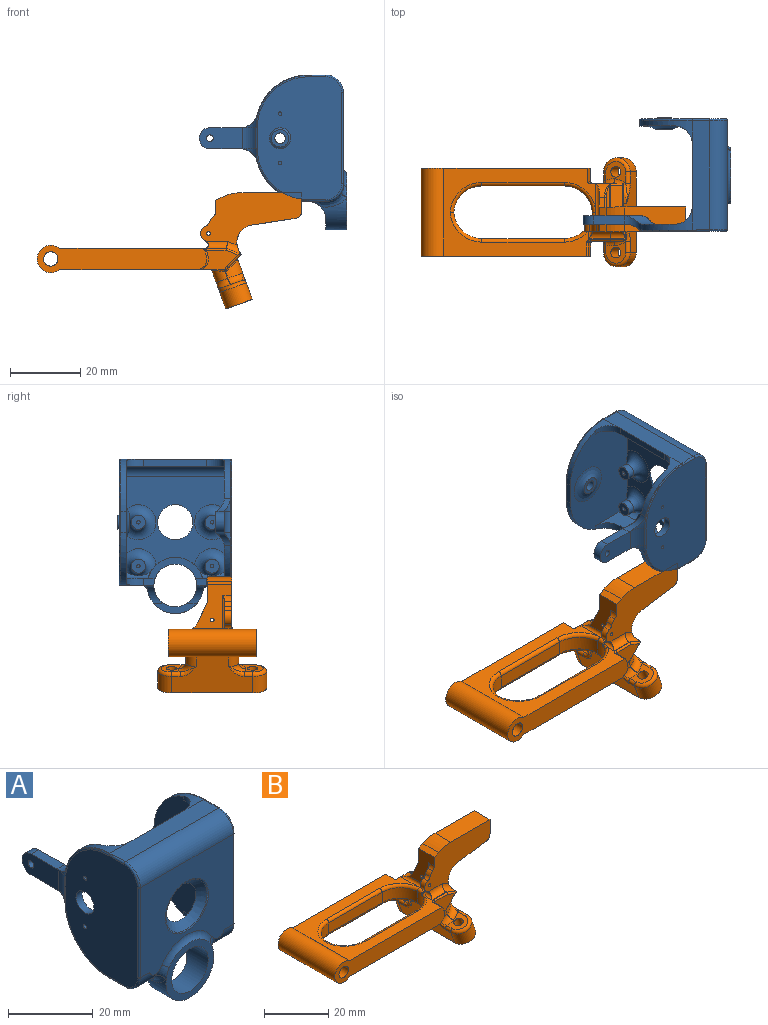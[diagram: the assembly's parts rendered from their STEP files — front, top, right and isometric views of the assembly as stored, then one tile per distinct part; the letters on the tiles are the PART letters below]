
ASSEMBLY  parts=2 mates=1
PART A: 112 faces, bbox 37.6x43.4x49.7 mm
  f0: plane 34.28x22.36mm, normal (1,0,0), area 579.8mm2, adj f18,f21,f30,f32,f33,f34,f36,f37
  f1: cylinder r=5mm len=6.53mm, axis (1,0,0), area 41.7mm2, adj f8,f9,f23,f66,f86,f87
  f2: cylinder r=5mm len=0.6mm, axis (1,0,0), area 0.1mm2, adj f9,f39,f89
  f3: plane 7.91x5.41mm, normal (0,0,-1), area 34.3mm2, adj f6,f20,f28,f70,f90
  f4: plane 3.24x2mm, normal (0,1,0), area 6mm2, adj f23,f30,f36,f80,f92
  f5: plane 10x8.24mm, normal (0,0,1), area 46.6mm2, adj f7,f28,f31,f35,f80,f82
  f6: cylinder r=5mm len=6.53mm, axis (1,0,0), area 41.7mm2, adj f3,f9,f39,f68,f89,f90
  f7: cylinder r=3mm len=6.99mm, axis (1,0,0), area 18.7mm2, adj f5,f31,f53,f81
  f8: cylinder r=2mm len=3.87mm, axis (0,1,0), area 0.6mm2, adj f1,f9,f44,f87
  f9: plane 31x27.5mm, normal (0,-1,0), area 595.5mm2, adj f1,f2,f6,f8,f27,f39,f44,f55
  f10: plane 1x1mm, normal (0,1,0), area 0.8mm2, adj f43
  f11: cylinder r=0.5mm len=5mm, axis (0,1,0), area 15.7mm2, adj f13,f40
  f12: cylinder r=2mm len=4mm, axis (0,1,0), area 25.1mm2, adj f13,f52
  f13: plane 4x4mm, normal (0,1,0), area 11.8mm2, adj f11,f12
  f14: plane 1x1mm, normal (0,1,0), area 0.8mm2, adj f17
  f15: cylinder r=2mm len=4mm, axis (0,1,0), area 25.1mm2, adj f16,f53
  f16: plane 4x4mm, normal (0,1,0), area 11.8mm2, adj f15,f17
  f17: cylinder r=0.5mm len=5mm, axis (0,1,0), area 15.7mm2, adj f14,f16
  f18: cylinder r=15mm len=14.52mm, axis (1,0,0), area 38.7mm2, adj f0,f25,f37,f97,f102,f103
  f19: cylinder r=15mm len=15mm, axis (1,0,0), area 40.7mm2, adj f25,f26,f31,f38,f73
  f20: cylinder r=15mm len=15mm, axis (-1,0,0), area 40.7mm2, adj f3,f26,f31,f35,f72
  f21: cylinder r=15mm len=14.52mm, axis (-1,0,0), area 38.7mm2, adj f0,f23,f36,f99,f100,f101
  f22: plane 35x24mm, normal (-1,0,0), area 711.2mm2, adj f56,f57,f58,f59,f60,f61,f62,f63
  f23: plane 8.1x5.41mm, normal (0,0,-1), area 34.6mm2, adj f1,f4,f21,f64,f86,f99
  f24: plane 35x24mm, normal (1,0,0), area 728.5mm2, adj f67,f68,f69,f70,f71,f72,f73,f74
  f25: plane 31.21x5.03mm, normal (0,0,1), area 155.3mm2, adj f18,f19,f27,f29,f61,f71,f97
  f26: plane 6x1.5mm, normal (0,1,0), area 9mm2, adj f19,f20,f31,f74
  f27: cylinder r=5mm len=31mm, axis (-1,0,0), area 243.5mm2, adj f9,f25,f63,f69
  f28: plane 3.24x2mm, normal (0,1,0), area 6mm2, adj f3,f5,f35,f80,f91
  f29: plane 18x2mm, normal (0,1,0), area 36mm2, adj f25,f32,f37,f38
  f30: plane 10x8.24mm, normal (0,0,1), area 46.6mm2, adj f0,f4,f36,f45,f80,f82
  f31: plane 34.28x23mm, normal (-1,0,0), area 580.8mm2, adj f5,f7,f19,f20,f26,f32,f33,f34
  f32: plane 28x10mm, normal (0,0,-1), area 150.7mm2, adj f0,f29,f31,f34,f37,f38
  f33: plane 28x25.2mm, normal (0,1,0), area 402mm2, adj f0,f31,f34,f50,f51,f52,f53,f54
  f34: cylinder r=3mm len=28mm, axis (-1,0,0), area 131.9mm2, adj f0,f31,f32,f33
  f35: cylinder r=5mm len=5mm, axis (0,0,-1), area 12.3mm2, adj f5,f20,f28,f31
  f36: cylinder r=5mm len=5mm, axis (0,0,1), area 12.3mm2, adj f0,f4,f21,f30
  f37: cylinder r=5mm len=5mm, axis (0,0,1), area 12.3mm2, adj f0,f18,f29,f32
  f38: cylinder r=5mm len=5mm, axis (0,0,-1), area 12.3mm2, adj f19,f29,f31,f32
  f39: cylinder r=2mm len=3.87mm, axis (0,1,0), area 0.6mm2, adj f2,f6,f9,f89
  f40: plane 1x1mm, normal (0,1,0), area 0.8mm2, adj f11
  f41: plane 4x4mm, normal (0,1,0), area 11.8mm2, adj f42,f43
  f42: cylinder r=2mm len=4mm, axis (0,1,0), area 25.1mm2, adj f41,f51
  f43: cylinder r=0.5mm len=5mm, axis (0,1,0), area 15.7mm2, adj f10,f41
  f44: cylinder r=5mm len=0.6mm, axis (1,0,0), area 0.1mm2, adj f8,f9,f87
  f45: cylinder r=3mm len=6.99mm, axis (1,0,0), area 18.7mm2, adj f0,f30,f50,f81
  f46: cylinder r=0.5mm len=5mm, axis (0,1,0), area 15.7mm2, adj f47,f49
  f47: plane 4x4mm, normal (0,1,0), area 11.8mm2, adj f46,f48
  f48: cylinder r=2mm len=4mm, axis (0,1,0), area 25.1mm2, adj f47,f50
  f49: plane 1x1mm, normal (0,1,0), area 0.8mm2, adj f46
  f50: torus R=5mm, axis (0,-1,0), area 66.5mm2, adj f0,f33,f45,f48,f81
  f51: torus R=5mm, axis (0,-1,0), area 83.9mm2, adj f0,f33,f42
  f52: torus R=5mm, axis (0,-1,0), area 83.9mm2, adj f12,f31,f33
  f53: torus R=5mm, axis (0,-1,0), area 66.5mm2, adj f7,f15,f31,f33,f81
  f54: cone r=5mm half-angle=45deg, axis (0,-1,0), area 97.6mm2, adj f33,f55
  f55: torus R=7.21mm, axis (0,-1,0), area 17.3mm2, adj f9,f54
  f56: cylinder r=3mm len=6mm, axis (-1,0,0), area 37.7mm2, adj f0,f22,f107
  f57: cylinder r=0.5mm len=2mm, axis (-1,0,0), area 6.3mm2, adj f0,f22
  f58: cylinder r=0.5mm len=2mm, axis (-1,0,0), area 6.3mm2, adj f0,f22
  f59: torus R=14.5mm, axis (1,0,0), area 10.2mm2, adj f22,f60,f61,f97
  f60: cylinder r=0.5mm len=6mm, axis (0,0,1), area 2.6mm2, adj f22,f59,f62,f98
  f61: cylinder r=0.5mm len=5mm, axis (0,-1,0), area 3.5mm2, adj f22,f25,f59,f63,f97
  f62: torus R=14.5mm, axis (1,0,0), area 10.2mm2, adj f22,f60,f64,f99
  f63: torus R=4.5mm, axis (1,0,0), area 5.9mm2, adj f22,f27,f61,f65
  f64: cylinder r=0.5mm len=5mm, axis (0,1,0), area 3.5mm2, adj f22,f23,f62,f66,f99
  f65: cylinder r=0.5mm len=26mm, axis (0,0,-1), area 20.4mm2, adj f9,f22,f63,f66
  f66: torus R=4.5mm, axis (1,0,0), area 5.9mm2, adj f1,f22,f64,f65
  f67: cylinder r=0.5mm len=26mm, axis (0,0,1), area 20.4mm2, adj f9,f24,f68,f69
  f68: torus R=4.5mm, axis (1,0,0), area 5.9mm2, adj f6,f24,f67,f70
  f69: torus R=4.5mm, axis (1,0,0), area 5.9mm2, adj f24,f27,f67,f71
  f70: cylinder r=0.5mm len=5mm, axis (0,-1,0), area 3.9mm2, adj f3,f24,f68,f72
  f71: cylinder r=0.5mm len=5mm, axis (0,1,0), area 3.9mm2, adj f24,f25,f69,f73
  f72: torus R=14.5mm, axis (1,0,0), area 18.3mm2, adj f20,f24,f70,f74
  f73: torus R=14.5mm, axis (1,0,0), area 18.3mm2, adj f19,f24,f71,f74
  f74: cylinder r=0.5mm len=6mm, axis (0,0,-1), area 4.7mm2, adj f24,f26,f72,f73
  f75: cylinder r=1.5mm len=3.5mm, axis (1,0,0), area 33mm2, adj f76,f79
  f76: plane 5x5mm, normal (-1,0,0), area 12.6mm2, adj f75,f77
  f77: torus R=5.5mm, axis (1,0,0), area 79.8mm2, adj f31,f76
  f78: cylinder r=2mm len=4mm, axis (-1,0,0), area 6.3mm2, adj f24,f79
  f79: plane 4x4mm, normal (1,0,0), area 5.5mm2, adj f75,f78
  f80: cylinder r=6.1mm len=12.2mm, axis (0,-1,0), area 261.4mm2, adj f4,f5,f28,f30,f82,f83,f84,f91
  f81: cylinder r=8mm len=15.49mm, axis (0,-1,0), area 56.2mm2, adj f7,f33,f45,f50,f53,f82
  f82: plane 15.49x6mm, normal (0,1,0), area 34.4mm2, adj f5,f30,f80,f81
  f83: plane 12.49x3mm, normal (0,1,0), area 20.9mm2, adj f80,f85,f91,f92
  f84: plane 16.13x16.13mm, normal (0,-1,0), area 84.2mm2, adj f80,f85,f87,f88,f89
  f85: cylinder r=8mm len=16mm, axis (0,-1,0), area 146.5mm2, adj f83,f84,f86,f90,f91,f92
  f86: bspline ~11.94x4.3mm, area 23.5mm2, adj f1,f23,f85,f87,f92
  f87: bspline ~4.41x3.22mm, area 7.4mm2, adj f1,f8,f44,f84,f86,f88
  f88: torus R=9.73mm, axis (0,-1,0), area 37.9mm2, adj f9,f84,f87,f89
  f89: bspline ~4.41x3.22mm, area 7.4mm2, adj f2,f6,f39,f84,f88,f90
  f90: bspline ~11.94x4.3mm, area 23.5mm2, adj f3,f6,f85,f89,f91
  f91: cylinder r=5mm len=5mm, axis (-1,0,0), area 15.1mm2, adj f28,f80,f83,f85,f90
  f92: cylinder r=5mm len=5mm, axis (1,0,0), area 15.1mm2, adj f4,f80,f83,f85,f86
  f93: plane 12.26x6.08mm, normal (-1,0,0), area 66.9mm2, adj f94,f95,f97,f98,f99,f101,f103,f104
  f94: plane 8.64x2.5mm, normal (0,0,1), area 21.6mm2, adj f93,f96,f103,f104
  f95: plane 8.64x2.5mm, normal (0,0,-1), area 21.6mm2, adj f93,f96,f101,f104
  f96: plane 15.91x6mm, normal (1,0,0), area 88.5mm2, adj f94,f95,f100,f102,f104,f105,f109,f110
  f97: torus R=18.74mm, axis (1,0,0), area 8.6mm2, adj f18,f25,f59,f61,f93,f98,f103
  f98: cylinder r=5mm len=6mm, axis (0,0,1), area 26.4mm2, adj f60,f93,f97,f99
  f99: torus R=18.74mm, axis (1,0,0), area 8.6mm2, adj f21,f23,f62,f64,f93,f98,f101
  f100: cylinder r=5mm len=9.15mm, axis (0,1,0), area 21.2mm2, adj f0,f21,f96,f101,f106,f109
  f101: cylinder r=5mm len=4.84mm, axis (-1,0,0), area 13.4mm2, adj f21,f93,f95,f99,f100
  f102: cylinder r=5mm len=9.15mm, axis (0,1,0), area 21.2mm2, adj f0,f18,f96,f103,f108,f111
  f103: cylinder r=5mm len=4.84mm, axis (1,0,0), area 13.4mm2, adj f18,f93,f94,f97,f102
  f104: cylinder r=3mm len=6mm, axis (1,0,0), area 23.6mm2, adj f93,f94,f95,f96
  f105: cylinder r=0.95mm len=2.5mm, axis (1,0,0), area 14.9mm2, adj f93,f96
  f106: cylinder r=2mm len=5.31mm, axis (0,0,-1), area 7.4mm2, adj f0,f100,f107,f109
  f107: bspline ~4.04x1.79mm, area 6.3mm2, adj f56,f106,f108,f110
  f108: cylinder r=2mm len=5.31mm, axis (0,0,-1), area 7.4mm2, adj f0,f102,f107,f111
  f109: cylinder r=4mm len=3.25mm, axis (0,0,-1), area 6.7mm2, adj f96,f100,f106,f110
  f110: bspline ~4.15x3.36mm, area 15.7mm2, adj f96,f107,f109,f111
  f111: cylinder r=4mm len=3.25mm, axis (0,0,-1), area 6.7mm2, adj f96,f102,f108,f110
PART B: 152 faces, bbox 76.2x32.6x34 mm
  f0: cylinder r=1.5mm len=6.66mm, axis (-0.34,0,0.94), area 56.5mm2, adj f109,f110
  f1: cylinder r=1.5mm len=6.66mm, axis (-0.34,0,0.94), area 56.5mm2, adj f108,f110
  f2: plane 23.9x12.3mm, normal (0.94,0,0.34), area 163.7mm2, adj f27,f29,f34,f35,f51,f110,f136,f137
  f3: plane 28.73x14.93mm, normal (0,-1,0), area 259.6mm2, adj f7,f25,f26,f58,f61,f62,f63,f64
  f4: plane 47.47x25.08mm, normal (0,0,1), area 417.3mm2, adj f12,f15,f17,f25,f36,f37,f44,f57
  f5: plane 8.14x3.73mm, normal (0,1,0), area 18.5mm2, adj f61,f62,f66,f77,f78,f79,f80,f106
  f6: plane 9.32x7.5mm, normal (0,1,0), area 26mm2, adj f68,f70,f72,f73,f100,f102
  f7: plane 12.74x11.14mm, normal (-1,0,0), area 77.9mm2, adj f3,f9,f59,f60,f61,f67,f76,f106
  f8: plane 7.78x7.52mm, normal (1,0,0), area 35.6mm2, adj f69,f72,f75,f76,f127,f130,f131
  f9: plane 6.44x3.25mm, normal (0,0.9,0.43), area 9.6mm2, adj f7,f59,f60,f127,f130
  f10: plane 47.5x25.19mm, normal (0,0,-1), area 406.7mm2, adj f12,f17,f39,f40,f41,f43,f46,f47
  f11: plane 10.49x0.17mm, normal (0,0,1), area 1.2mm2, adj f14,f69,f70,f96
  f12: plane 48.35x7.78mm, normal (0,-1,0), area 277.3mm2, adj f4,f10,f16,f38,f40,f56,f57,f81
  f13: plane 15.46x3.8mm, normal (0.72,0,-0.69), area 22.3mm2, adj f15,f24,f49,f51,f53,f97,f101,f103
  f14: plane 10.23x3.48mm, normal (0.37,0,0.93), area 38.4mm2, adj f11,f68,f96,f101
  f15: plane 4.17x1.68mm, normal (0.37,0,0.93), area 1.1mm2, adj f4,f13,f26,f145
  f16: cylinder r=2.05mm len=25mm, axis (0,1,0), area 322mm2, adj f12,f17
  f17: plane 48.35x7.78mm, normal (0,1,0), area 277.3mm2, adj f4,f10,f16,f36,f41,f56,f57,f81
  f18: plane 23.48x4mm, normal (0,1,0), area 93.9mm2, adj f21,f22,f86,f121
  f19: plane 23.48x4mm, normal (0,-1,0), area 93.9mm2, adj f20,f23,f87,f124
  f20: cylinder r=8mm len=7.98mm, axis (0,0,-1), area 48.3mm2, adj f19,f21,f83,f85,f122
  f21: cylinder r=8mm len=7.98mm, axis (0,0,1), area 48.7mm2, adj f18,f20,f82,f84,f117,f118,f119,f120
  f22: cylinder r=8mm len=7.98mm, axis (0,0,-1), area 48.3mm2, adj f18,f23,f88,f123
  f23: cylinder r=8mm len=7.98mm, axis (0,0,1), area 48.3mm2, adj f19,f22,f89,f125
  f24: plane 4.57x1.24mm, normal (0.86,0,0.51), area 3mm2, adj f13,f26,f64,f103,f105
  f25: cylinder r=2mm len=6.51mm, axis (-1,0,0), area 18.1mm2, adj f3,f4,f26,f65,f78
  f26: cylinder r=2mm len=5.28mm, axis (-0.93,0,0.37), area 11.9mm2, adj f3,f15,f24,f25,f64
  f27: cylinder r=4mm len=9.23mm, axis (-0.34,0,0.94), area 62.8mm2, adj f2,f31,f110,f135
  f28: cylinder r=4mm len=2.06mm, axis (0.34,0,-0.94), area 0.3mm2, adj f32,f34,f54,f112
  f29: cylinder r=4mm len=9.23mm, axis (-0.34,0,0.94), area 62.8mm2, adj f2,f31,f110,f140
  f30: cylinder r=4mm len=2.06mm, axis (0.34,0,-0.94), area 0.3mm2, adj f33,f35,f46,f115
  f31: plane 23x10.91mm, normal (-0.94,0,-0.34), area 184.5mm2, adj f27,f29,f32,f33,f50,f110,f133,f134
  f32: cylinder r=3mm len=4.56mm, axis (0.34,0,-0.94), area 14.8mm2, adj f28,f31,f52,f113
  f33: cylinder r=3mm len=4.56mm, axis (0.34,0,-0.94), area 14.8mm2, adj f30,f31,f48,f116
  f34: cylinder r=5mm len=5.59mm, axis (0.34,0,-0.94), area 24mm2, adj f2,f28,f53,f55,f111
  f35: cylinder r=5mm len=5.59mm, axis (0.34,0,-0.94), area 24mm2, adj f2,f30,f47,f49,f114
  f36: plane 3.77x1.97mm, normal (0.94,0,0.34), area 7.9mm2, adj f4,f17,f41,f44
  f37: plane 9.39x5.56mm, normal (0,1,0), area 37.1mm2, adj f4,f44,f45,f60,f91,f92,f93,f94
  f38: plane 3.77x1.65mm, normal (0.94,0,0.34), area 6.6mm2, adj f12,f40,f42,f148
  f39: plane 10.03x5.5mm, normal (0,-1,0), area 37.5mm2, adj f10,f42,f43,f143,f144,f145,f146
  f40: cylinder r=3mm len=4.03mm, axis (0,-1,0), area 21.7mm2, adj f10,f12,f38,f43
  f41: cylinder r=3mm len=4.03mm, axis (0,-1,0), area 21.7mm2, adj f10,f17,f36,f45
  f42: cylinder r=0.5mm len=1.82mm, axis (0.34,0,-0.94), area 1.2mm2, adj f38,f39,f43,f147
  f43: torus R=3.5mm, axis (0,1,0), area 4.1mm2, adj f10,f39,f40,f42
  f44: cylinder r=0.5mm len=2.15mm, axis (0.34,0,-0.94), area 1.6mm2, adj f4,f36,f37,f45
  f45: torus R=3.5mm, axis (0,1,0), area 3.8mm2, adj f37,f41,f44,f90
  f46: bspline ~0.52x0.51mm, area 0.1mm2, adj f10,f30,f47,f48
  f47: bspline ~0.55x0.53mm, area 0.2mm2, adj f10,f35,f46,f49,f143
  f48: bspline ~4.26x3.5mm, area 3.9mm2, adj f10,f33,f46,f50
  f49: bspline ~5.4x3.96mm, area 4.7mm2, adj f13,f35,f47,f51,f143
  f50: cylinder r=0.5mm len=9.14mm, axis (0,1,0), area 5.2mm2, adj f10,f31,f48,f52,f82,f83
  f51: cylinder r=0.5mm len=5.11mm, axis (0,-1,0), area 2.9mm2, adj f2,f13,f49,f53
  f52: bspline ~4.26x3.5mm, area 3.8mm2, adj f10,f32,f50,f54,f92
  f53: bspline ~5.4x3.96mm, area 4.7mm2, adj f13,f34,f51,f55,f95
  f54: bspline ~0.5x0.37mm, area 0.1mm2, adj f28,f52,f55,f93
  f55: bspline ~0.51x0.47mm, area 0.2mm2, adj f34,f53,f54,f94,f95
  f56: cylinder r=5mm len=25mm, axis (0,-1,0), area 3.3mm2, adj f10,f12,f17,f81
  f57: cylinder r=5mm len=25mm, axis (0,-1,0), area 3.3mm2, adj f4,f12,f17,f81
  f58: plane 19.52x4.98mm, normal (0,0,-1), area 39.9mm2, adj f3,f63,f73,f75,f98,f128,f129
  f59: plane 24.5x7.39mm, normal (0,1,0), area 128.7mm2, adj f7,f9,f126,f127,f128,f149,f150,f151
  f60: cylinder r=5mm len=4.08mm, axis (1,0,0), area 11.3mm2, adj f7,f9,f37,f67,f96,f131,f132
  f61: cylinder r=2mm len=2.5mm, axis (0,-1,0), area 4.1mm2, adj f3,f5,f7,f62,f106
  f62: cylinder r=3mm len=2mm, axis (0,-1,0), area 3.6mm2, adj f3,f5,f61,f79
  f63: plane 11.68x2.87mm, normal (0.15,0,-0.99), area 20.8mm2, adj f3,f58,f64,f98,f100
  f64: cylinder r=5mm len=7.47mm, axis (0,-1,0), area 15.2mm2, adj f3,f24,f26,f63,f102,f104
  f65: cylinder r=1mm len=4.33mm, axis (0,1,0), area 4.6mm2, adj f4,f25,f66,f78,f117,f118
  f66: cylinder r=1mm len=1.73mm, axis (1,0,0), area 1.9mm2, adj f4,f5,f65,f107,f118
  f67: cylinder r=1mm len=11.23mm, axis (0,-1,0), area 15.2mm2, adj f4,f7,f60,f107
  f68: cylinder r=1mm len=4.16mm, axis (0.93,0,-0.37), area 5.6mm2, adj f6,f14,f70,f103,f104,f105
  f69: cylinder r=1mm len=10.52mm, axis (0,1,0), area 14.3mm2, adj f8,f11,f71,f96,f132
  f70: cylinder r=1mm len=1mm, axis (1,0,0), area 0.3mm2, adj f6,f11,f68,f71
  f71: sphere r=1mm, area 1.6mm2, adj f69,f70,f72
  f72: cylinder r=1mm len=6.46mm, axis (0,0,-1), area 10.2mm2, adj f6,f8,f71,f74
  f73: cylinder r=1mm len=18.96mm, axis (-1,0,0), area 24.3mm2, adj f6,f58,f74,f98
  f74: sphere r=1mm, area 1.6mm2, adj f72,f73,f75
  f75: cylinder r=1mm len=1.97mm, axis (0,1,0), area 3.1mm2, adj f8,f58,f74,f127
  f76: cylinder r=0.5mm len=2mm, axis (1,0,0), area 6.3mm2, adj f7,f8
  f77: cylinder r=2.23mm len=4.03mm, axis (0,-1,0), area 10mm2, adj f3,f5,f78,f79
  f78: cylinder r=2mm len=2.27mm, axis (0,1,0), area 3.5mm2, adj f3,f5,f25,f65,f77
  f79: cylinder r=2mm len=2mm, axis (0,-1,0), area 3.3mm2, adj f3,f5,f62,f77
  f80: cylinder r=0.5mm len=2mm, axis (0,-1,0), area 6.3mm2, adj f3,f5
  f81: cylinder r=3.89mm len=25mm, axis (0,1,0), area 439.6mm2, adj f12,f17,f56,f57
  f82: bspline ~3.15x1.2mm, area 3.1mm2, adj f21,f50,f83,f84
  f83: bspline ~3.15x1.2mm, area 3.1mm2, adj f20,f50,f82,f85
  f84: torus R=9mm, axis (0,0,-1), area 16.3mm2, adj f10,f21,f82,f86
  f85: torus R=9mm, axis (0,0,-1), area 16.3mm2, adj f10,f20,f83,f87
  f86: cylinder r=1mm len=23.48mm, axis (1,0,0), area 36.9mm2, adj f10,f18,f84,f88
  f87: cylinder r=1mm len=23.48mm, axis (-1,0,0), area 36.9mm2, adj f10,f19,f85,f89
  f88: torus R=9mm, axis (0,0,-1), area 19.9mm2, adj f10,f22,f86,f89
  f89: torus R=9mm, axis (0,0,-1), area 19.9mm2, adj f10,f23,f87,f88
  f90: bspline ~2.79x1mm, area 0.7mm2, adj f10,f45,f91
  f91: cylinder r=0.5mm len=3.61mm, axis (1,0,0), area 2.8mm2, adj f10,f37,f90,f92
  f92: bspline ~3.61x0.65mm, area 1.4mm2, adj f37,f52,f91,f93
  f93: bspline ~1.11x0.5mm, area 0.1mm2, adj f37,f54,f92,f94
  f94: bspline ~1.56x0.51mm, area 0.1mm2, adj f37,f55,f93,f95
  f95: bspline ~1.69x1.67mm, area 0.5mm2, adj f37,f53,f55,f94,f97
  f96: cylinder r=0.5mm len=4.82mm, axis (-0.93,0,0.37), area 3.3mm2, adj f11,f14,f37,f60,f69,f99,f132
  f97: cylinder r=0.5mm len=3.62mm, axis (0.69,0,0.72), area 3.6mm2, adj f13,f37,f95,f99
  f98: bspline ~11.12x1.72mm, area 4.9mm2, adj f58,f63,f73,f100
  f99: sphere r=0.5mm, area 0.4mm2, adj f96,f97,f101
  f100: cylinder r=0.5mm len=2.15mm, axis (0.99,0,0.15), area 1.6mm2, adj f6,f63,f98,f102
  f101: cylinder r=0.5mm len=10.23mm, axis (0,-1,0), area 10mm2, adj f13,f14,f99,f103
  f102: torus R=5.5mm, axis (0,1,0), area 7.1mm2, adj f6,f64,f100,f104
  f103: bspline ~1.26x1.13mm, area 0.9mm2, adj f13,f24,f68,f101,f105
  f104: bspline ~1.45x1.13mm, area 0.7mm2, adj f64,f68,f102,f105
  f105: bspline ~0.74x0.73mm, area 0.4mm2, adj f24,f68,f103,f104
  f106: cylinder r=0.5mm len=9.46mm, axis (0,0,1), area 6.9mm2, adj f5,f7,f61,f107
  f107: bspline ~1.19x1mm, area 0.5mm2, adj f66,f67,f106
  f108: plane 6.2x5.64mm, normal (-0.34,0,0.94), area 20.6mm2, adj f1,f114,f115,f116,f139,f140,f141
  f109: plane 6.2x5.64mm, normal (-0.34,0,0.94), area 20.6mm2, adj f0,f111,f112,f113,f134,f135,f136
  f110: plane 31x7.52mm, normal (0.34,0,-0.94), area 220.1mm2, adj f0,f1,f2,f27,f29,f31
  f111: torus R=7mm, axis (-0.34,0,0.94), area 17.1mm2, adj f34,f109,f112,f137
  f112: torus R=2mm, axis (-0.34,0,0.94), area 0.3mm2, adj f28,f109,f111,f113
  f113: torus R=5mm, axis (-0.34,0,0.94), area 12.6mm2, adj f32,f109,f112,f133
  f114: torus R=7mm, axis (-0.34,0,0.94), area 17.1mm2, adj f35,f108,f115,f138
  f115: torus R=2mm, axis (-0.34,0,0.94), area 0.3mm2, adj f30,f108,f114,f116
  f116: torus R=5mm, axis (-0.34,0,0.94), area 12.6mm2, adj f33,f108,f115,f142
  f117: bspline ~2.71x1.53mm, area 2.4mm2, adj f21,f65,f118,f119
  f118: bspline ~1.8x1.76mm, area 1.5mm2, adj f21,f65,f66,f117,f120
  f119: torus R=9mm, axis (0,0,-1), area 11.7mm2, adj f4,f21,f117,f121
  f120: torus R=9mm, axis (0,0,-1), area 3.7mm2, adj f4,f21,f118,f122
  f121: cylinder r=1mm len=23.48mm, axis (1,0,0), area 36.9mm2, adj f4,f18,f119,f123
  f122: torus R=9mm, axis (0,0,-1), area 19.9mm2, adj f4,f20,f120,f124
  f123: torus R=9mm, axis (0,0,-1), area 19.9mm2, adj f4,f22,f121,f125
  f124: cylinder r=1mm len=23.48mm, axis (-1,0,0), area 36.9mm2, adj f4,f19,f122,f125
  f125: torus R=9mm, axis (0,0,-1), area 19.9mm2, adj f4,f23,f123,f124
  f126: plane 6.97x5.39mm, normal (1,0,0), area 37.6mm2, adj f3,f59,f129,f149
  f127: torus R=3mm, axis (0,-1,0), area 5.3mm2, adj f8,f9,f59,f75,f128,f130
  f128: cylinder r=2mm len=21.5mm, axis (1,0,0), area 64.4mm2, adj f58,f59,f127,f129
  f129: cylinder r=2mm len=6.97mm, axis (0,-1,0), area 18.7mm2, adj f3,f58,f126,f128
  f130: cylinder r=0.5mm len=6.3mm, axis (0,-0.43,0.9), area 5.3mm2, adj f8,f9,f127,f131
  f131: torus R=5.5mm, axis (1,0,0), area 1.5mm2, adj f8,f60,f130,f132
  f132: bspline ~3.6x1.68mm, area 1.5mm2, adj f60,f69,f96,f131
  f133: bspline ~5.43x2.82mm, area 3.1mm2, adj f31,f113,f134
  f134: cylinder r=1mm len=2.35mm, axis (0,-1,0), area 3.7mm2, adj f31,f109,f133,f135
  f135: torus R=3mm, axis (-0.34,0,0.94), area 17.9mm2, adj f27,f109,f134,f136
  f136: cylinder r=1mm len=3.2mm, axis (0,-1,0), area 5mm2, adj f2,f109,f135,f137
  f137: bspline ~6.76x2.82mm, area 3.4mm2, adj f2,f111,f136
  f138: bspline ~6.76x2.82mm, area 3.4mm2, adj f2,f114,f139
  f139: cylinder r=1mm len=3.2mm, axis (0,-1,0), area 5mm2, adj f2,f108,f138,f140
  f140: torus R=3mm, axis (-0.34,0,0.94), area 17.9mm2, adj f29,f108,f139,f141
  f141: cylinder r=1mm len=2.35mm, axis (0,-1,0), area 3.7mm2, adj f31,f108,f140,f142
  f142: bspline ~4.8x2.82mm, area 3.1mm2, adj f31,f116,f141
  f143: bspline ~2.04x2.03mm, area 0.7mm2, adj f10,f39,f47,f49,f144
  f144: cylinder r=0.5mm len=4.15mm, axis (-0.69,0,-0.72), area 3.9mm2, adj f13,f39,f143,f145
  f145: cylinder r=0.5mm len=4.36mm, axis (0.93,0,-0.37), area 3.2mm2, adj f15,f39,f144,f146
  f146: cylinder r=0.5mm len=5.73mm, axis (1,0,0), area 4.5mm2, adj f4,f39,f145,f147
  f147: bspline ~1.25x1.17mm, area 0.8mm2, adj f4,f42,f146,f148
  f148: cylinder r=0.5mm len=3.77mm, axis (0,1,0), area 2.3mm2, adj f4,f12,f38,f147
  f149: plane 17.23x6.97mm, normal (0,0,1), area 120mm2, adj f3,f59,f126,f150
  f150: cylinder r=12.5mm len=6.97mm, axis (0,-1,0), area 38.9mm2, adj f3,f59,f149,f151
  f151: plane 6.97x1.88mm, normal (-0.43,0,0.9), area 14.5mm2, adj f3,f7,f59,f150
PLACE A rot(axis=(0,0,1),90deg) t=(182.03,-15.1,88.64)mm
PLACE B t=(105.74,-13.11,60.52)mm
MATE parallel A.f93 <-> B.f6  axis (0,-1,0) through (154.61,-29.1,94.89)mm
